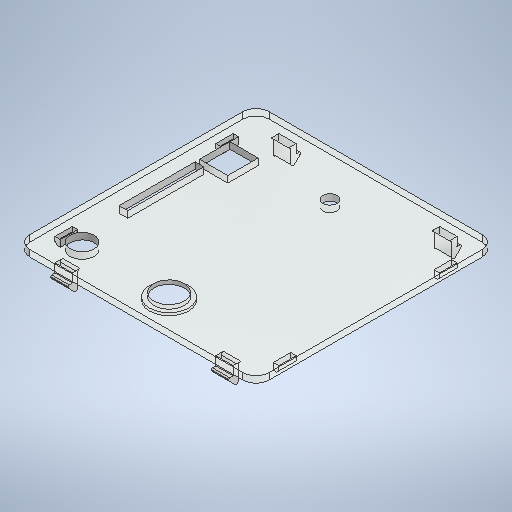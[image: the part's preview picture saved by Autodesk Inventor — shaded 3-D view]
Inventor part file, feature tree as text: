
AUTODESK INVENTOR PART (.ipt)
format: ipt  version: 2025 (Build 290162000, 162)  size: 456,192 bytes
history: native  units: mm
features: sketch x9, extrude x7, fillet x7, chamfer x3, other x1
ambient origin geometry x8: Origin, YZ Plane, XZ Plane, XY Plane, X Axis, Y Axis, Z Axis, Center Point
bodies: Solid1 (feature_tree)
feature tree (27):
  extrude  "Extrusion1"  Depth=110.0mm
  fillet  "Fillet1"  Radius=6.0mm
  extrude  "Extrusion2"  Depth=6.0mm
  extrude  "Extrusion3"  Depth=14.0mm
  extrude  "Extrusion4"  Depth=3.0mm TaperAngle=0.0deg
  chamfer  "Chamfer1"  Distance=8.0mm
  fillet  "Fillet2"  Radius=2.5mm
  fillet  "Fillet3"  Radius=3.5mm
  extrude  "Extrusion5"  Depth=14.0mm
  chamfer  "Chamfer2"  Distance=74.0mm
  fillet  "Fillet4"  Radius=100.5mm
  fillet  "Fillet5"  Radius=8.1mm
  fillet  "Fillet6"  Radius=4.0mm
  fillet  "Fillet7"  [1 undecoded]
  extrude  "Extrusion6"  TaperAngle=0.0deg  [1 undecoded]
  extrude  "Extrusion7"  Depth=4.0mm
  chamfer  "Chamfer3"  Distance=2.0mm
  sketch  "Sketch1"  dims[d0=110.0mm d1=110.0mm d2=6.0mm]
  sketch  "Sketch2"  dims[d6=21.0mm d7=14.0mm]
  sketch  "Sketch3"  dims[d11=13.0mm]
  sketch  "Sketch Rectangular Pattern1"  dims[d3=3.0mm d4=0.0mm d5=6.0mm]
  sketch  "Sketch4"  dims[d12=4.0mm]
  sketch  "Sketch5"  dims[d13=35.0mm]
  sketch  "Sketch6"  dims[d14=9.0mm]
  sketch  "Sketch Rectangular Pattern2"  dims[d8=9.0mm d9=3.0mm d10=0.0mm]
  sketch  "Sketch7"  dims[d15=2.0mm d20=8.0mm d21=2.5mm d22=3.5mm d23=14.0mm d24=20.0mm d26=74.0mm d27=20.0mm d29=100.5mm d32=8.1mm d33=0.0mm d34=4.0mm d35=0.0mm d36=0.0mm d37=4.0mm d38=2.0mm d39=0.0mm d40=3.0mm d41=2.0mm d42=45.0deg d43=1.0mm d44=0.5mm d45=4.05mm d46=2.0mm d47=0.0mm d48=3.0mm d49=2.0mm d50=45.0deg d51=1.0mm d52=0.5mm d53=1.0mm d54=1.0mm d55=6.5mm d56=55.0mm d57=21.0mm d58=11.0mm d59=15.0mm d60=15.0mm d61=14.0mm d62=15.0mm d63=55.0mm d64=18.0mm d65=1.2mm d66=0.0mm d67=8.0mm d68=2.5mm d69=3.5mm d70=14.0mm d71=20.0mm d73=74.0mm d74=20.0mm d76=100.5mm d79=5.0mm d80=0.0mm d81=8.0mm d82=1.0mm d83=2.0mm d84=45.0deg]
  other  "Finish1"
note: 2 required parameter values undecoded (feature->parameter linkage not recoverable at this tier; creation-order binding heuristic only, values carry confidence <= 0.55)
